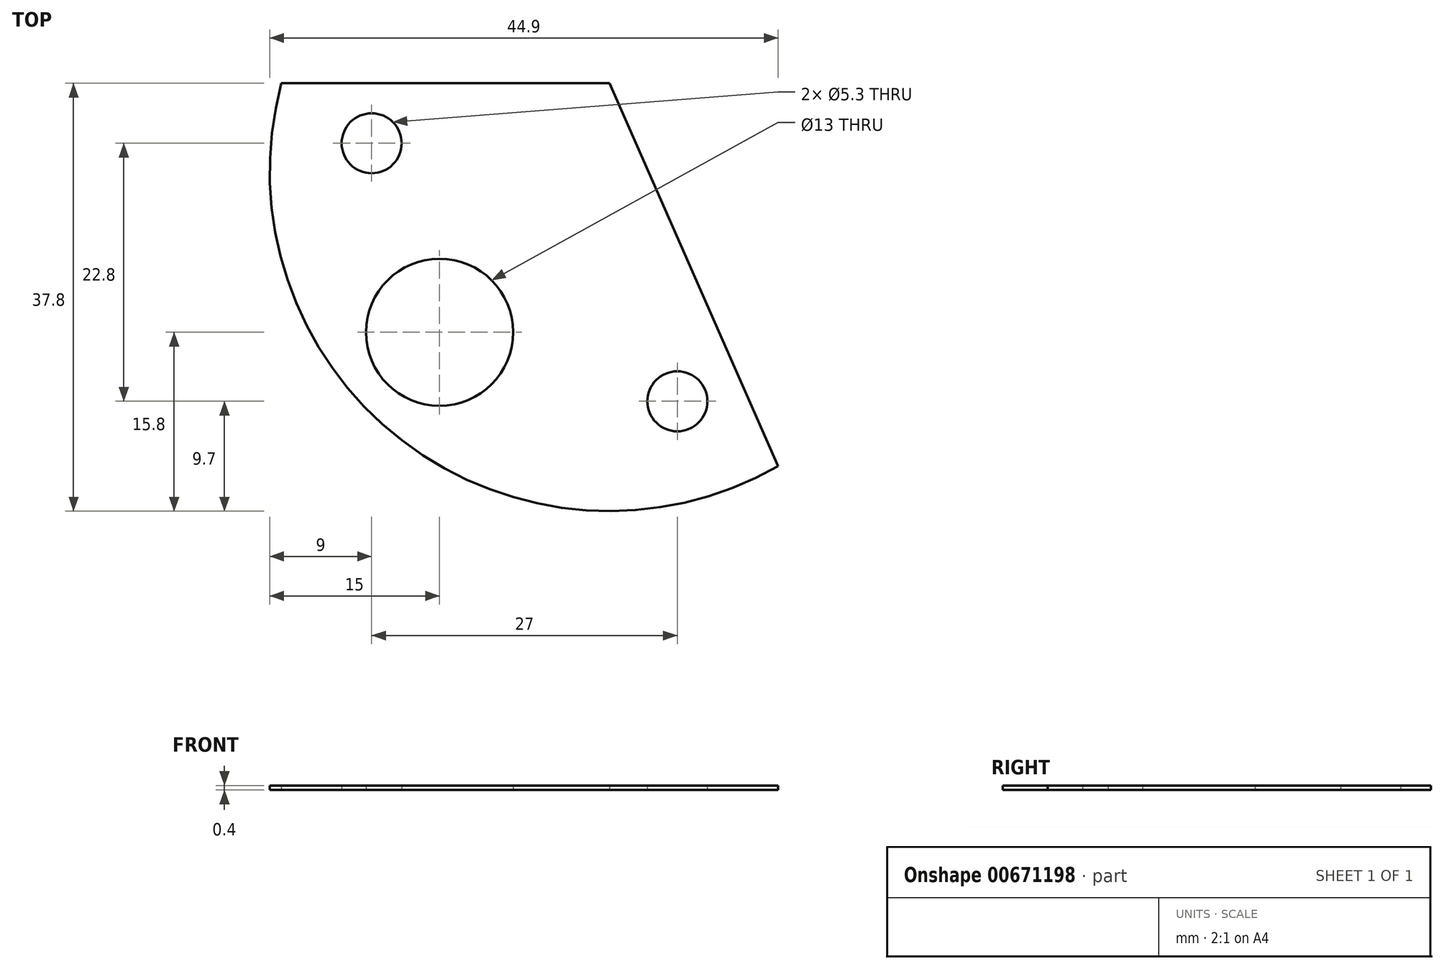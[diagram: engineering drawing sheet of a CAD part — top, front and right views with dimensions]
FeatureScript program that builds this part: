
annotation { "Feature Type Name" : "Feature", "Feature Type Description" : "" }
export const myFeature = defineFeature(function(context is Context, id is Id, definition is map)
    precondition{}
    {
        {
            var Q0;
            Q0=qCreatedBy(makeId("Top.planeOp"),FACE);
            var sketch = newSketch(context, id + "F0", { "sketchPlane" : qUnion([Q0])});
            skArc(sketch, "E0", {"start": v(-28.97, 7.8) * mm, "mid": v(-18.32, -23.75) * mm, "end": v(14.9, -26.04) * mm});
            skCircle(sketch, "E1", {"center": v(-21, 2.5) * mm, "radius": 2.65 * mm});
            skCircle(sketch, "E2", {"center": v(6, -20.3) * mm, "radius": 2.65 * mm});
            skCircle(sketch, "E3", {"center": v(-15, -14.2) * mm, "radius": 6.5 * mm});
            skLineSegment(sketch, "E4", {"start": v(-28.97, 7.8) * mm, "end": v(0, 7.8) * mm});
            skLineSegment(sketch, "E5", {"start": v(0, 7.8) * mm, "end": v(14.9, -26.04) * mm});
            skSolve(sketch);
        }
        {
            var Q0;
            Q0=makeQuery(id+"F0.imprint","IMPRINT",FACE,{"disambiguationData":[TD([[makeQuery(id+"F0.imprint","IMPRINT",EDGE,{"derivedFrom":sQuery(id+"F0.wireOp",EDGE,"E0")}),1.0]])]});
            extrude(context, id + "F1", {"entities" : qUnion([Q0]), "depth" : 0.4 * mm, "offsetDistance" : 25 * mm});
        }
    });
